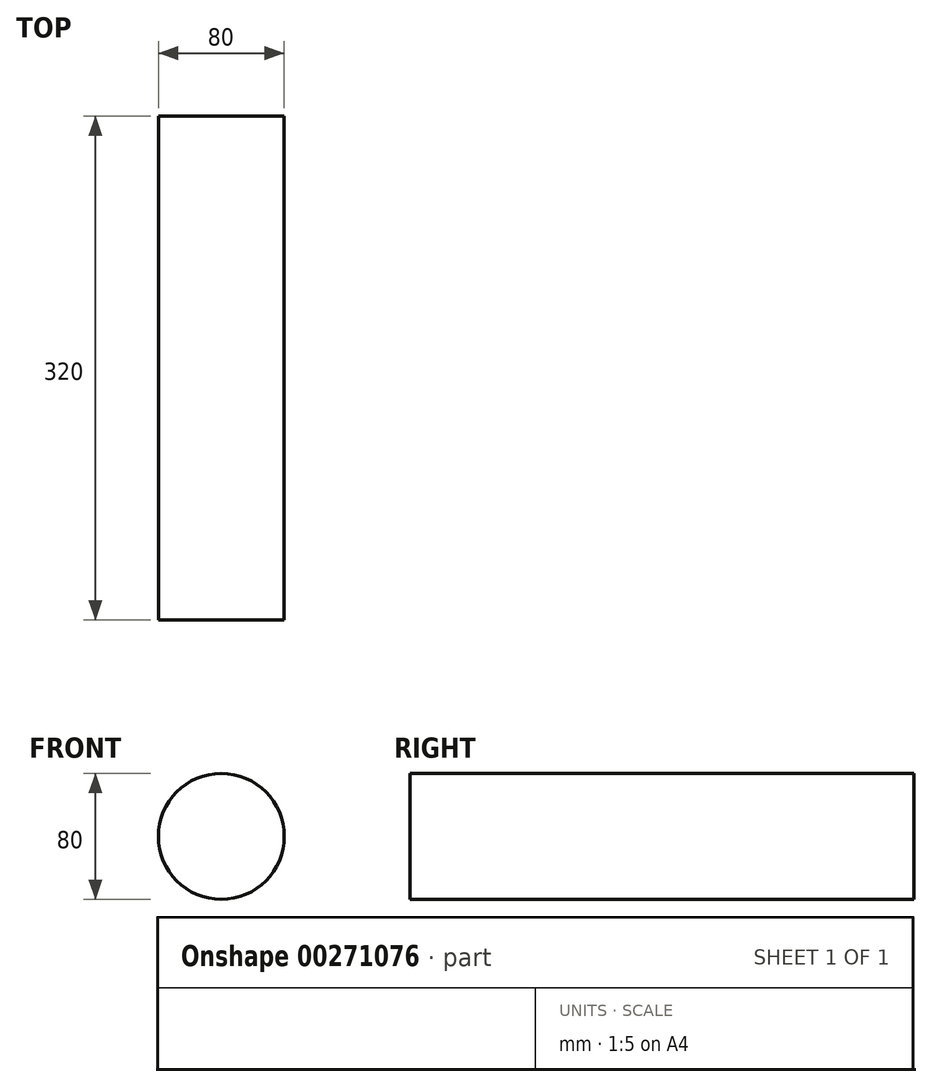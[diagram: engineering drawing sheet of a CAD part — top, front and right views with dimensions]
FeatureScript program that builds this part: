
annotation { "Feature Type Name" : "Feature", "Feature Type Description" : "" }
export const myFeature = defineFeature(function(context is Context, id is Id, definition is map)
    precondition{}
    {
        {
            var Q0;
            Q0=qCreatedBy(makeId("Front.planeOp"),FACE);
            var sketch = newSketch(context, id + "F0", { "sketchPlane" : qUnion([Q0])});
            skCircle(sketch, "E0", {"center": v(-80, 0) * mm, "radius": 40 * mm});
            skPoint(sketch, "E1.first.point", {"position": v(-64.77, 36.99) * mm});
            skPoint(sketch, "E1.third.point", {"position": v(-46.36, 107.9) * mm});
            skSolve(sketch);
        }
        {
            var Q0;
            Q0=makeQuery(id+"F0.imprint","IMPRINT",FACE,{"disambiguationData":[TD([[makeQuery(id+"F0.imprint","IMPRINT",EDGE,{"derivedFrom":sQuery(id+"F0.wireOp",EDGE,"E0")}),1.0]])]});
            extrude(context, id + "F1", {"entities" : qUnion([Q0]), "depth" : 320 * mm});
        }
    });
